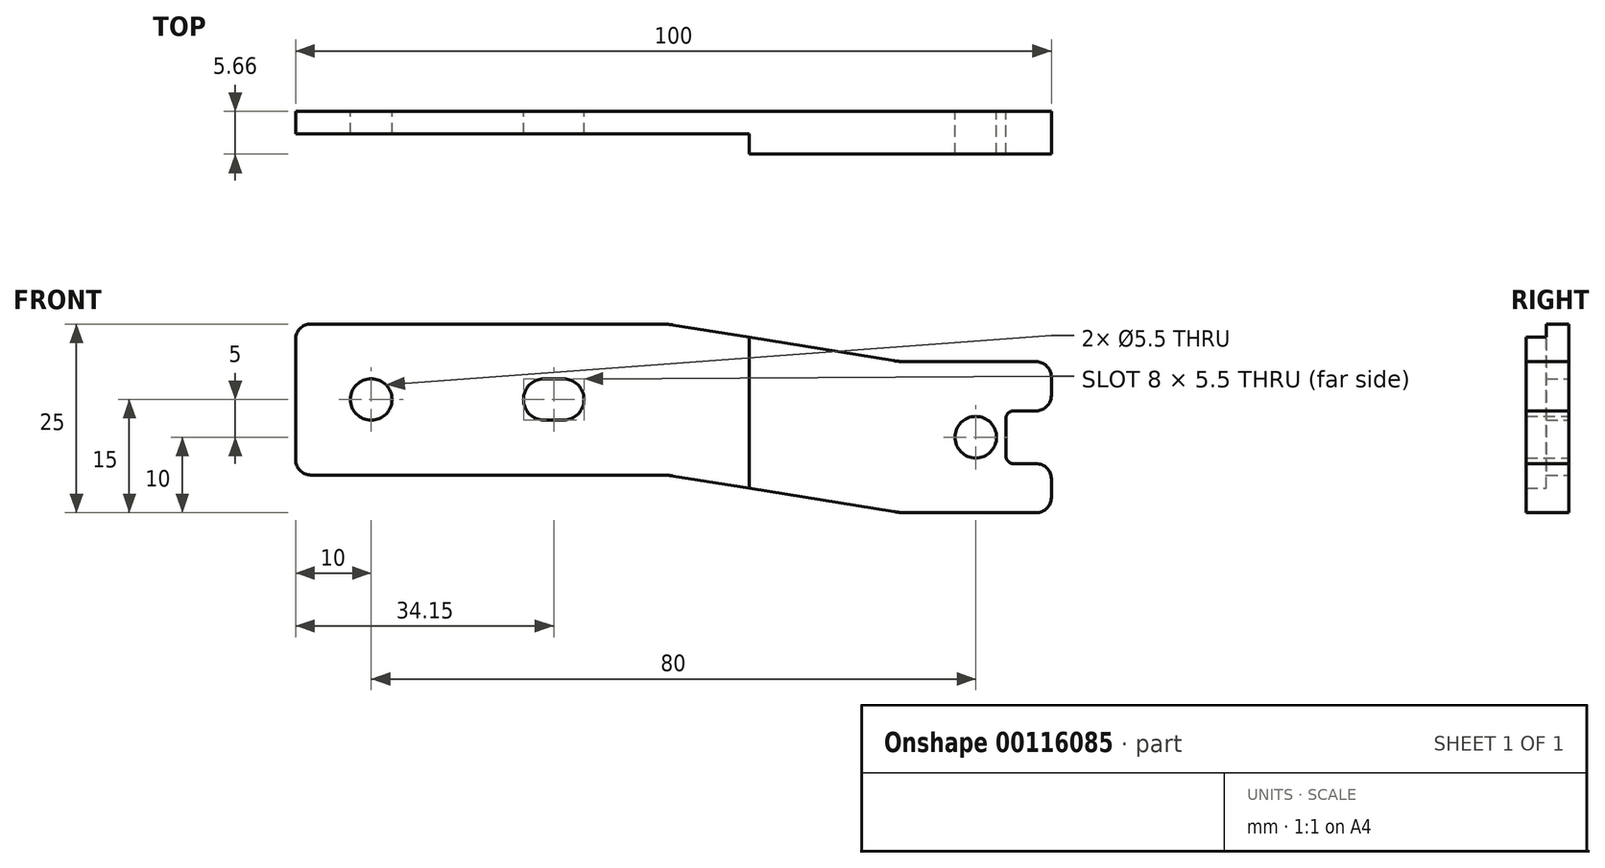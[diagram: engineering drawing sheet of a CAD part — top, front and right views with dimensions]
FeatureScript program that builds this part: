
annotation { "Feature Type Name" : "Feature", "Feature Type Description" : "" }
export const myFeature = defineFeature(function(context is Context, id is Id, definition is map)
    precondition{}
    {
        {
            var Q0;
            Q0=qCreatedBy(makeId("Front.planeOp"),FACE);
            var sketch = newSketch(context, id + "F0", { "sketchPlane" : qUnion([Q0])});
            skLineSegment(sketch, "E0", {"start": v(0, 24.1) * mm, "end": v(0, 0) * mm, "construction": true});
            skLineSegment(sketch, "E1", {"start": v(-60, 0) * mm, "end": v(0, 0) * mm, "construction": true});
            skLineSegment(sketch, "E2", {"start": v(-60, 10) * mm, "end": v(-60, -10) * mm});
            skCircle(sketch, "E3", {"center": v(-50, 0) * mm, "radius": 2.75 * mm});
            skCircle(sketch, "E4", {"center": v(-25.85, 0) * mm, "radius": 2.75 * mm, "construction": true});
            skCircle(sketch, "E5", {"center": v(30, -5) * mm, "radius": 2.75 * mm});
            skLineSegment(sketch, "E6", {"start": v(20, -15) * mm, "end": v(40, -15) * mm});
            skLineSegment(sketch, "E7", {"start": v(40, -15) * mm, "end": v(40, -8.5) * mm});
            skLineSegment(sketch, "E8", {"start": v(40, 5) * mm, "end": v(20, 5) * mm});
            skLineSegment(sketch, "E9", {"start": v(40, -5) * mm, "end": v(30, -5) * mm, "construction": true});
            skLineSegment(sketch, "E10", {"start": v(-60, 10) * mm, "end": v(-10.85, 10) * mm});
            skLineSegment(sketch, "E11", {"start": v(-10.85, -10) * mm, "end": v(-60, -10) * mm});
            skLineSegment(sketch, "E12", {"start": v(20, -15) * mm, "end": v(-10.85, -10) * mm});
            skLineSegment(sketch, "E13", {"start": v(20, 5) * mm, "end": v(-10.85, 10) * mm});
            skLineSegment(sketch, "E14", {"start": v(34, -1.5) * mm, "end": v(40, -1.5) * mm});
            skLineSegment(sketch, "E15", {"start": v(34, -8.5) * mm, "end": v(40, -8.5) * mm});
            skLineSegment(sketch, "E16.trimOffspring", {"start": v(40, -1.5) * mm, "end": v(40, 5) * mm});
            skLineSegment(sketch, "E17", {"start": v(34, -1.5) * mm, "end": v(34, -8.5) * mm});
            skArc(sketch, "E18", {"start": v(-27.1, 2.75) * mm, "mid": v(-29.85, 0) * mm, "end": v(-27.1, -2.75) * mm});
            skArc(sketch, "E19", {"start": v(-24.6, -2.75) * mm, "mid": v(-21.85, 0) * mm, "end": v(-24.6, 2.75) * mm});
            skLineSegment(sketch, "E20", {"start": v(-24.6, 0) * mm, "end": v(-27.1, 0) * mm, "construction": true});
            skLineSegment(sketch, "E21", {"start": v(-24.6, -2.75) * mm, "end": v(-27.1, -2.75) * mm});
            skLineSegment(sketch, "E22.MirrorCS", {"start": v(-24.6, 2.75) * mm, "end": v(-27.1, 2.75) * mm});
            skLineSegment(sketch, "E23", {"start": v(0, -11.76) * mm, "end": v(0, 8.24) * mm});
            skSolve(sketch);
        }
        {
            var Q0;
            Q0=makeQuery(id+"F0.imprint","IMPRINT",FACE,{"disambiguationData":[TD([[makeQuery(id+"F0.imprint","IMPRINT",EDGE,{"derivedFrom":sQuery(id+"F0.wireOp",EDGE,"E2")}),1.0]])]});
            var Q1;
            Q1=makeQuery(id+"F0.imprint","IMPRINT",FACE,{"disambiguationData":[TD([[makeQuery(id+"F0.imprint","IMPRINT",EDGE,{"derivedFrom":sQuery(id+"F0.wireOp",EDGE,"E5")}),-1.0]])]});
            extrude(context, id + "F1", {"entities" : qUnion([Q0, Q1]), "depth" : 3 * mm, "offsetDistance" : 25 * mm});
        }
        {
            var Q0;
            Q0=makeQuery(id+"F1.opExtrude","CAP_FACE",FACE,{"disambiguationData":[OSD([sQuery(id+"F0.wireOp",EDGE,"E2"),sQuery(id+"F0.wireOp",EDGE,"E3"),sQuery(id+"F0.wireOp",EDGE,"E4"),sQuery(id+"F0.wireOp",EDGE,"E5"),sQuery(id+"F0.wireOp",EDGE,"E6"),sQuery(id+"F0.wireOp",EDGE,"E7"),sQuery(id+"F0.wireOp",EDGE,"E8"),sQuery(id+"F0.wireOp",EDGE,"E10"),sQuery(id+"F0.wireOp",EDGE,"E11"),sQuery(id+"F0.wireOp",EDGE,"E12"),sQuery(id+"F0.wireOp",EDGE,"E13")])],"isStart":false});
            var sketch = newSketch(context, id + "F2", { "sketchPlane" : qUnion([Q0])});
            skLineSegment(sketch, "E24.bottom", {"start": v(40, -15) * mm, "end": v(20, -15) * mm});
            skLineSegment(sketch, "E24.top", {"start": v(40, 5) * mm, "end": v(20, 5) * mm});
            skLineSegment(sketch, "E24.left", {"start": v(40, -15) * mm, "end": v(40, 5) * mm});
            skLineSegment(sketch, "E24.right", {"start": v(20, -15) * mm, "end": v(20, 5) * mm});
            skCircle(sketch, "E25", {"center": v(30, -5) * mm, "radius": 2.75 * mm});
            skLineSegment(sketch, "E26.0", {"start": v(0, -11.76) * mm, "end": v(0, 8.24) * mm});
            skSolve(sketch);
        }
        {
            var Q0;
            Q0=makeQuery(id+"F2.imprint","IMPRINT",FACE,{"disambiguationData":[TD([[makeQuery(id+"F2.imprint","IMPRINT",EDGE,{"derivedFrom":sQuery(id+"F2.wireOp",EDGE,"E24.bottom")}),1.0]])]});
            var Q1;
            {var subQ0=sQuery(id+"F2.wireOp",EDGE,"E24.right");Q1=makeQuery(id+"F2.imprint","IMPRINT",FACE,{"disambiguationData":[TD([[makeQuery(id+"F2.imprint","IMPRINT",EDGE,{"derivedFrom":subQ0}),1.0]])]});}
            extrude(context, id + "F3", {"entities" : qUnion([Q0, Q1]), "operationType" : NewBodyOperationType.ADD, "depth" : 2.66 * mm, "offsetDistance" : 25 * mm});
        }
        {
            var Q0;
            {var subQ0=sQuery(id+"F0.wireOp",EDGE,"E17");var subQ1=sQuery(id+"F0.wireOp",EDGE,"E14");Q0=makeQuery(id+"F3.boolean.opBoolean","MERGE",EDGE,{"derivedFrom":[makeQuery(id+"F1.opExtrude","SWEPT_EDGE",EDGE,{"disambiguationData":[OSD([subQ1,subQ0])]}),makeQuery(id+"F3.opExtrude","SWEPT_EDGE",EDGE,{"disambiguationData":[OSD([subQ1,subQ0])]})]});}
            var Q1;
            {var subQ0=sQuery(id+"F0.wireOp",EDGE,"E17");var subQ1=sQuery(id+"F0.wireOp",EDGE,"E15");Q1=makeQuery(id+"F3.boolean.opBoolean","MERGE",EDGE,{"derivedFrom":[makeQuery(id+"F1.opExtrude","SWEPT_EDGE",EDGE,{"disambiguationData":[OSD([subQ1,subQ0])]}),makeQuery(id+"F3.opExtrude","SWEPT_EDGE",EDGE,{"disambiguationData":[OSD([subQ1,subQ0])]})]});}
            fillet(context, id + "F4", {"entities" : qUnion([Q0, Q1]), "radius" : 1 * mm, "tangentPropagation" : true, "allowEdgeOverflow" : false});
        }
        {
            var Q0;
            Q0=makeQuery(id+"F3.boolean.opBoolean","MERGE",EDGE,{"derivedFrom":[makeQuery(id+"F1.opExtrude","SWEPT_EDGE",EDGE,{"disambiguationData":[OSD([sQuery(id+"F0.wireOp",EDGE,"E8"),sQuery(id+"F0.wireOp",EDGE,"E16.trimOffspring")])]}),makeQuery(id+"F3.opExtrude","SWEPT_EDGE",EDGE,{"disambiguationData":[OSD([sQuery(id+"F2.wireOp",EDGE,"E24.top"),sQuery(id+"F2.wireOp",EDGE,"E24.left")])]})]});
            var Q1;
            {var subQ0=sQuery(id+"F0.wireOp",EDGE,"E15");Q1=makeQuery(id+"F3.boolean.opBoolean","MERGE",EDGE,{"derivedFrom":[makeQuery(id+"F1.opExtrude","SWEPT_EDGE",EDGE,{"disambiguationData":[OSD([sQuery(id+"F0.wireOp",EDGE,"E7"),subQ0])]}),makeQuery(id+"F3.opExtrude","SWEPT_EDGE",EDGE,{"disambiguationData":[OSD([subQ0,sQuery(id+"F2.wireOp",EDGE,"E24.left")])]})]});}
            var Q2;
            {var subQ0=sQuery(id+"F0.wireOp",EDGE,"E14");Q2=makeQuery(id+"F3.boolean.opBoolean","MERGE",EDGE,{"derivedFrom":[makeQuery(id+"F1.opExtrude","SWEPT_EDGE",EDGE,{"disambiguationData":[OSD([subQ0,sQuery(id+"F0.wireOp",EDGE,"E16.trimOffspring")])]}),makeQuery(id+"F3.opExtrude","SWEPT_EDGE",EDGE,{"disambiguationData":[OSD([subQ0,sQuery(id+"F2.wireOp",EDGE,"E24.left")])]})]});}
            var Q3;
            Q3=makeQuery(id+"F3.boolean.opBoolean","MERGE",EDGE,{"derivedFrom":[makeQuery(id+"F1.opExtrude","SWEPT_EDGE",EDGE,{"disambiguationData":[OSD([sQuery(id+"F0.wireOp",EDGE,"E6"),sQuery(id+"F0.wireOp",EDGE,"E7")])]}),makeQuery(id+"F3.opExtrude","SWEPT_EDGE",EDGE,{"disambiguationData":[OSD([sQuery(id+"F2.wireOp",EDGE,"E24.bottom"),sQuery(id+"F2.wireOp",EDGE,"E24.left")])]})]});
            var Q4;
            Q4=makeQuery(id+"F1.opExtrude","SWEPT_EDGE",EDGE,{"disambiguationData":[OSD([sQuery(id+"F0.wireOp",EDGE,"E2"),sQuery(id+"F0.wireOp",EDGE,"E10")])]});
            var Q5;
            Q5=makeQuery(id+"F1.opExtrude","SWEPT_EDGE",EDGE,{"disambiguationData":[OSD([sQuery(id+"F0.wireOp",EDGE,"E2"),sQuery(id+"F0.wireOp",EDGE,"E11")])]});
            fillet(context, id + "F5", {"entities" : qUnion([Q0, Q1, Q2, Q3, Q4, Q5]), "radius" : 2 * mm, "tangentPropagation" : true, "allowEdgeOverflow" : false});
        }
        {
            var Q0;
            Q0=makeQuery(id+"F1.opExtrude","SWEPT_EDGE",EDGE,{"disambiguationData":[OSD([sQuery(id+"F0.wireOp",EDGE,"E10"),sQuery(id+"F0.wireOp",EDGE,"E13")])]});
            var Q1;
            Q1=makeQuery(id+"F1.opExtrude","SWEPT_EDGE",EDGE,{"disambiguationData":[OSD([sQuery(id+"F0.wireOp",EDGE,"E8"),sQuery(id+"F0.wireOp",EDGE,"E13")])]});
            var Q2;
            Q2=makeQuery(id+"F1.opExtrude","SWEPT_EDGE",EDGE,{"disambiguationData":[OSD([sQuery(id+"F0.wireOp",EDGE,"E11"),sQuery(id+"F0.wireOp",EDGE,"E12")])]});
            var Q3;
            Q3=makeQuery(id+"F1.opExtrude","SWEPT_EDGE",EDGE,{"disambiguationData":[OSD([sQuery(id+"F0.wireOp",EDGE,"E6"),sQuery(id+"F0.wireOp",EDGE,"E12")])]});
            fillet(context, id + "F6", {"entities" : qUnion([Q0, Q1, Q2, Q3]), "radius" : 10 * mm, "tangentPropagation" : true, "allowEdgeOverflow" : false});
        }
    });
